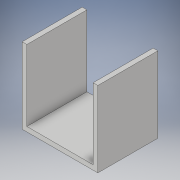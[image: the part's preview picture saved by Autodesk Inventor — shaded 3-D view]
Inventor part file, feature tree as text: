
AUTODESK INVENTOR PART (.ipt)
format: ipt  version: 2017 (Build 210142000, 142)  size: 98,816 bytes
history: native  units: in
note: dims shown in document units (in); Inventor stores cm internally (conversion verified against a paired STEP export)
features: sketch x2, extrude x1
ambient origin geometry x8: Origin, YZ Plane, XZ Plane, XY Plane, X Axis, Y Axis, Z Axis, Center Point
bodies: Solid1 (feature_tree)
feature tree (3):
  sketch  "Sketch1"  dims[d2=0.079in d3=1.26in]
  sketch  "Sketch2"  dims[d5=1.0in d6=0.0in]
  extrude  "Extrusion1"  Depth=1.26in
